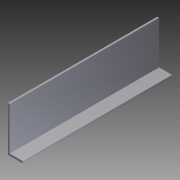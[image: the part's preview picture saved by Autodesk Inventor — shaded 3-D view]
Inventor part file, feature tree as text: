
AUTODESK INVENTOR PART (.ipt)
format: ipt  version: 2012 (Build 160160000, 160)  size: 73,728 bytes
history: native  units: in
note: dims shown in document units (in); Inventor stores cm internally (conversion verified against a paired STEP export)
features: extrude x1, sketch x1
ambient origin geometry x8: Origin, YZ Plane, XZ Plane, XY Plane, X Axis, Y Axis, Z Axis, Center Point
bodies: Solid1 (feature_tree)
feature tree (2):
  extrude  "Extrusion1"  Depth=1.0in
  sketch  "Sketch1"  dims[d0=3.0in d1=1.0in d2=0.125in d3=0.125in d4=10.0in d5=0.0in]
